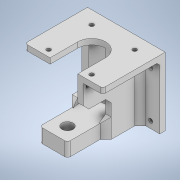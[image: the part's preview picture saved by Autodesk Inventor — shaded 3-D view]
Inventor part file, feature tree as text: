
AUTODESK INVENTOR PART (.ipt)
format: ipt  version: 2022 (Build 260153000, 153)  size: 316,928 bytes
history: native  units: mm
features: sketch x14, extrude x13, chamfer x4, hole x3, other x1, fillet x1
ambient origin geometry x8: Origin, YZ Plane, XZ Plane, XY Plane, X Axis, Y Axis, Z Axis, Center Point
bodies: Body1 (feature_tree)
feature tree (36):
  other  "Sólido1"
  sketch  "Esboço1"  dims[d0=56.0mm d1=10.0mm]
  extrude  "Extrusão1"  Depth=10.0mm
  extrude  "Extrusão2"  Depth=4.0mm TaperAngle=0.0deg
  hole  "Furo1"  [1 undecoded]
  hole  "Furo2"  [1 undecoded]
  extrude  "Extrusão3"  Depth=22.0mm
  extrude  "Extrusão4"  Depth=15.5mm
  sketch  "Esboço6"  dims[d25=25.0mm d26=39.0mm d27=0.0mm]
  extrude  "Extrusão5"  Depth=20.0mm
  extrude  "Extrusão6"  Depth=3.0mm
  extrude  "Extrusão7"  Depth=3.0mm
  extrude  "Extrusão8"  Depth=20.0mm TaperAngle=0.0deg
  extrude  "Extrusão9"  Depth=14.0mm TaperAngle=0.0deg
  extrude  "Extrusão10"  Depth=14.0mm TaperAngle=0.0deg
  chamfer  "Chanfro2"  Distance=39.0mm
  fillet  "Arredondamento1"  Radius=10.0mm
  hole  "Furo3"  [1 undecoded]
  chamfer  "Chanfro3"  Distance=2.0mm
  extrude  "Extrusão11"  Depth=33.0mm
  extrude  "Extrusão12"  Depth=4.0mm TaperAngle=45.0deg
  chamfer  "Chanfro4"  Distance=2.5mm
  extrude  "Extrusão14"  Depth=4.0mm
  chamfer  "Chanfro5"  Distance=5.0mm
  sketch  "Esboço2"  dims[d2=20.0mm d3=4.0mm d4=0.0mm]
  sketch  "Esboço3"  dims[d5=52.426mm d6=0.0mm]
  sketch  "Esboço4"  dims[d10=8.0mm d11=6.0mm d12=4.0mm d13=2.0mm d14=90.0deg d15=8.0mm d16=20.594885mm]
  sketch  "Esboço5"  dims[d17=3.0mm d18=6.0mm d19=4.0mm d20=2.0mm d21=90.0deg d22=8.0mm d23=20.594885mm d24=10.0mm]
  sketch  "Esboço7"  dims[d28=22.0mm d29=0.0mm d30=15.5mm]
  sketch  "Esboço8"  dims[d31=15.5mm d32=15.5mm]
  sketch  "Esboço9"  dims[d33=15.5mm d34=20.0mm]
  sketch  "Esboço10"  dims[d35=0.0mm d36=0.0mm d37=3.0mm]
  sketch  "Esboço11"  dims[d38=3.0mm d39=3.0mm]
  sketch  "Esboço12"  dims[d40=3.0mm d41=20.0mm d42=0.0mm]
  sketch  "Esboço13"  dims[d43=4.0mm d44=14.0mm d45=0.0mm]
  sketch  "Esboço15"  dims[d46=4.0mm d47=14.0mm d48=0.0mm d49=39.0mm d50=0.0mm d51=10.0mm d52=0.0mm d53=4.0mm d54=2.0mm d55=45.0deg d56=2.0mm d57=33.0mm d58=3.0mm d59=6.0mm d60=4.0mm d61=2.0mm d62=90.0deg d63=8.0mm d64=20.594885mm d65=4.0mm d66=2.0mm d67=45.0deg d68=2.5mm d69=4.0mm d70=5.0mm d71=2.5mm d72=4.0mm d73=5.0mm d74=2.0mm d75=0.0mm d76=2.5mm d77=4.0mm d78=5.0mm d79=2.5mm d80=4.0mm d81=5.0mm d82=2.0mm d83=0.0mm d84=2.0mm d85=2.0mm d86=45.0deg d87=15.5mm d88=15.5mm d91=10.0mm d92=0.0mm d94=2.0mm d95=2.0mm d96=45.0deg]
note: 3 required parameter values undecoded (feature->parameter linkage not recoverable at this tier; creation-order binding heuristic only, values carry confidence <= 0.55)
